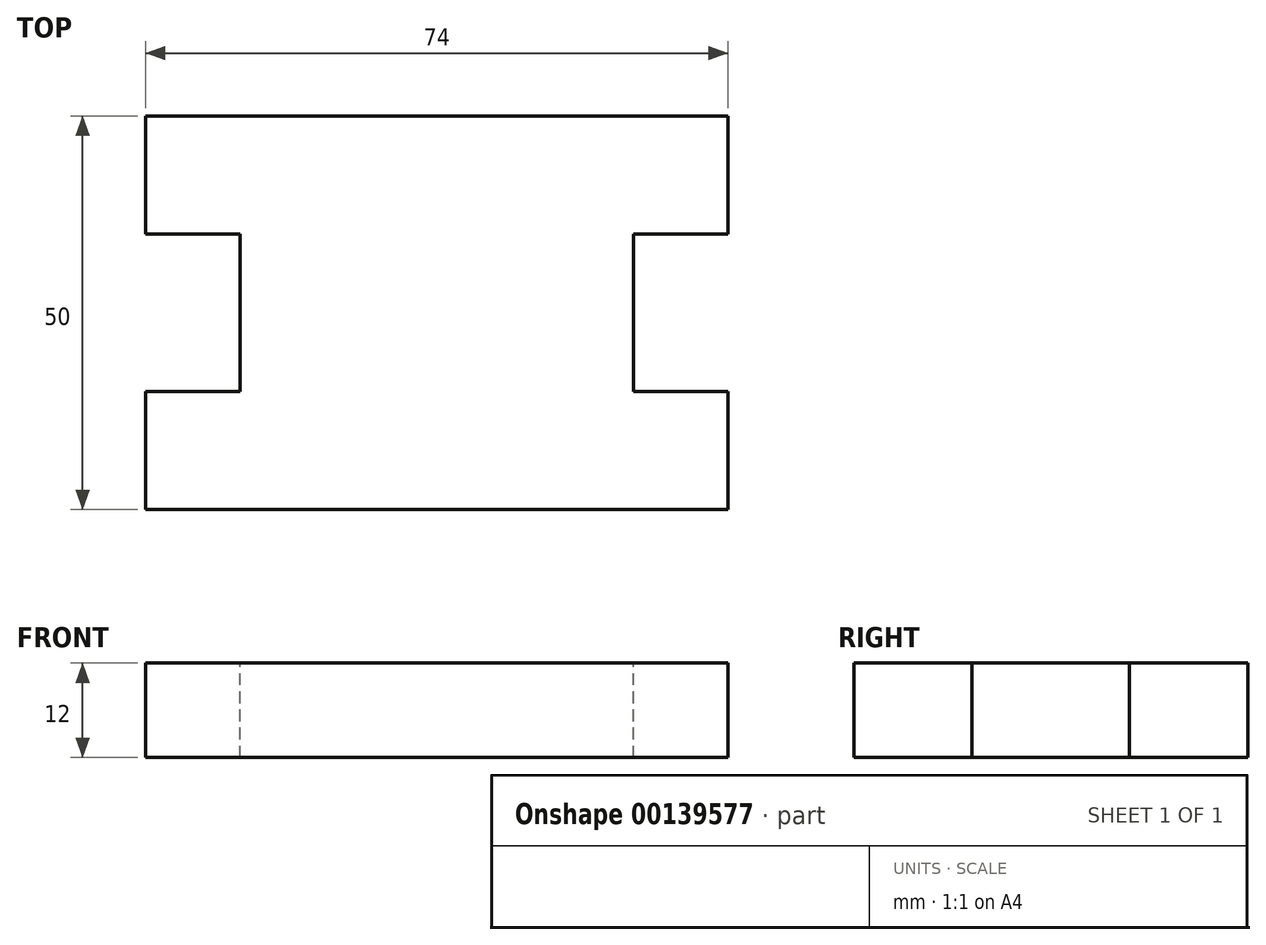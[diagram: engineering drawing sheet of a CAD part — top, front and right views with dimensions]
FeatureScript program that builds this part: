
annotation { "Feature Type Name" : "Feature", "Feature Type Description" : "" }
export const myFeature = defineFeature(function(context is Context, id is Id, definition is map)
    precondition{}
    {
        {
            var Q0;
            Q0=qCreatedBy(makeId("Top.planeOp"),FACE);
            var sketch = newSketch(context, id + "F0", { "sketchPlane" : qUnion([Q0])});
            skLineSegment(sketch, "E0.bottom", {"start": v(-49.73, 20.68) * mm, "end": v(24.27, 20.68) * mm});
            skLineSegment(sketch, "E0.top", {"start": v(-49.73, -29.32) * mm, "end": v(24.27, -29.32) * mm});
            skLineSegment(sketch, "E0.left", {"start": v(-49.73, 20.68) * mm, "end": v(-49.73, -29.32) * mm});
            skLineSegment(sketch, "E0.right", {"start": v(24.27, 20.68) * mm, "end": v(24.27, -29.32) * mm});
            skSolve(sketch);
        }
        {
            var Q0;
            Q0 = qSketchRegion(id + "F0", true);
            extrude(context, id + "F1", {"entities" : qUnion([Q0]), "depth" : 12 * mm});
        }
        {
            var Q0;
            Q0=makeQuery(id+"F1.opExtrude","CAP_FACE",FACE,{"disambiguationData":[OSD([sQuery(id+"F0.wireOp",EDGE,"E0.bottom"),sQuery(id+"F0.wireOp",EDGE,"E0.top"),sQuery(id+"F0.wireOp",EDGE,"E0.left"),sQuery(id+"F0.wireOp",EDGE,"E0.right")])],"isStart":false});
            var sketch = newSketch(context, id + "F2", { "sketchPlane" : qUnion([Q0])});
            skLineSegment(sketch, "E1.bottom", {"start": v(-49.73, 5.68) * mm, "end": v(-37.73, 5.68) * mm});
            skLineSegment(sketch, "E1.top", {"start": v(-49.73, -14.32) * mm, "end": v(-37.73, -14.32) * mm});
            skLineSegment(sketch, "E1.left", {"start": v(-49.73, 5.68) * mm, "end": v(-49.73, -14.32) * mm});
            skLineSegment(sketch, "E1.right", {"start": v(-37.73, 5.68) * mm, "end": v(-37.73, -14.32) * mm});
            skLineSegment(sketch, "E2.bottom", {"start": v(24.27, 5.68) * mm, "end": v(12.27, 5.68) * mm});
            skLineSegment(sketch, "E2.top", {"start": v(24.27, -14.32) * mm, "end": v(12.27, -14.32) * mm});
            skLineSegment(sketch, "E2.left", {"start": v(24.27, 5.68) * mm, "end": v(24.27, -14.32) * mm});
            skLineSegment(sketch, "E2.right", {"start": v(12.27, 5.68) * mm, "end": v(12.27, -14.32) * mm});
            skSolve(sketch);
        }
        {
            var Q0;
            Q0=makeQuery(id+"F2.imprint","IMPRINT",FACE,{"disambiguationData":[TD([[makeQuery(id+"F2.imprint","IMPRINT",EDGE,{"derivedFrom":sQuery(id+"F2.wireOp",EDGE,"E1.bottom")}),-1.0]])]});
            var Q1;
            Q1=makeQuery(id+"F2.imprint","IMPRINT",FACE,{"disambiguationData":[TD([[makeQuery(id+"F2.imprint","IMPRINT",EDGE,{"derivedFrom":sQuery(id+"F2.wireOp",EDGE,"E2.bottom")}),1.0]])]});
            extrude(context, id + "F3", {"entities" : qUnion([Q0, Q1]), "operationType" : NewBodyOperationType.REMOVE, "endBound" : BoundingType.THROUGH_ALL, "oppositeDirection" : true, "depth" : 25 * mm});
        }
    });
